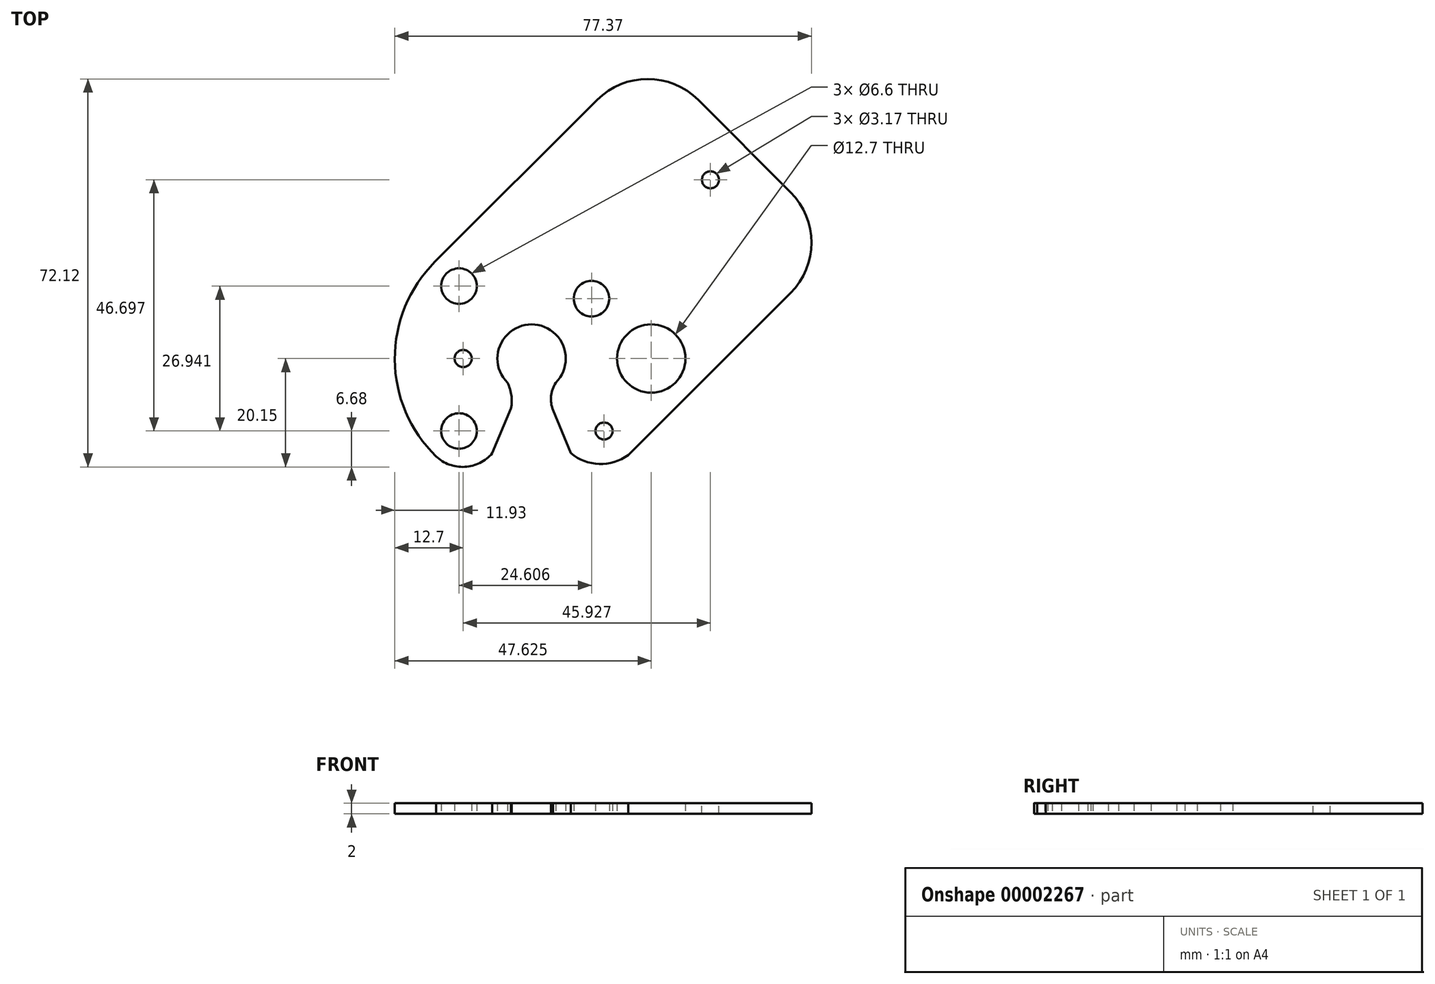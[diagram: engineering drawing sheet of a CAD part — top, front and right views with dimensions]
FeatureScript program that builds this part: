
annotation { "Feature Type Name" : "Feature", "Feature Type Description" : "" }
export const myFeature = defineFeature(function(context is Context, id is Id, definition is map)
    precondition{}
    {
        {
            var Q0;
            Q0=qCreatedBy(makeId("Top.planeOp"),FACE);
            var sketch = newSketch(context, id + "F0", { "sketchPlane" : qUnion([Q0])});
            skCircle(sketch, "E0", {"center": v(0, 0) * mm, "radius": 25.4 * mm});
            skCircle(sketch, "E1", {"center": v(0, 0) * mm, "radius": 6.35 * mm});
            skCircle(sketch, "E2", {"center": v(0, 0) * mm, "radius": 19.05 * mm, "construction": true});
            skLineSegment(sketch, "E3", {"start": v(0, 25.4) * mm, "end": v(0, -25.4) * mm, "construction": true});
            skLineSegment(sketch, "E4", {"start": v(25.4, 0) * mm, "end": v(-25.4, 0) * mm});
            skLineSegment(sketch, "E5", {"start": v(0, 0) * mm, "end": v(-26.94, -26.94) * mm});
            skLineSegment(sketch, "E6.2.0", {"start": v(0, 0) * mm, "end": v(26.94, 26.94) * mm, "construction": true});
            skLineSegment(sketch, "E6.3.0", {"start": v(0, 0) * mm, "end": v(-26.94, 26.94) * mm, "construction": true});
            skPoint(sketch, "E7", {"position": v(13.47, 13.47) * mm});
            skPoint(sketch, "E8", {"position": v(-13.47, 13.47) * mm});
            skPoint(sketch, "E9", {"position": v(13.47, -13.47) * mm});
            skPoint(sketch, "E10", {"position": v(-13.47, -13.47) * mm});
            skLineSegment(sketch, "E11", {"start": v(0, 0) * mm, "end": v(9.72, -23.47) * mm});
            skLineSegment(sketch, "E12.MirrorCS", {"start": v(-17.96, 17.96) * mm, "end": v(17.96, -17.96) * mm, "construction": true});
            skLineSegment(sketch, "E13.MirrorCS", {"start": v(0, 0) * mm, "end": v(-9.72, -23.47) * mm});
            skPoint(sketch, "E14", {"position": v(-7.3, -17.6) * mm});
            skPoint(sketch, "E15", {"position": v(7.3, -17.6) * mm});
            skArc(sketch, "E16", {"start": v(-17.96, -17.96) * mm, "mid": v(-12.55, -20.14) * mm, "end": v(-7.3, -17.6) * mm});
            skArc(sketch, "E17", {"start": v(7.3, -17.6) * mm, "mid": v(12.56, -19.59) * mm, "end": v(17.96, -17.96) * mm});
            skCircle(sketch, "E18", {"center": v(13.47, 13.47) * mm, "radius": 3.3 * mm, "construction": true});
            skCircle(sketch, "E19", {"center": v(-13.47, 13.47) * mm, "radius": 3.3 * mm});
            skCircle(sketch, "E20", {"center": v(-13.47, -13.47) * mm, "radius": 3.3 * mm});
            skCircle(sketch, "E21", {"center": v(13.47, -13.47) * mm, "radius": 1.59 * mm});
            skCircle(sketch, "E22", {"center": v(-12.7, 0) * mm, "radius": 1.59 * mm});
            skCircle(sketch, "E23", {"center": v(22.23, 0) * mm, "radius": 6.35 * mm});
            skPoint(sketch, "E24", {"position": v(18.37, 5.05) * mm});
            skPoint(sketch, "E25", {"position": v(18.37, -5.05) * mm});
            skPoint(sketch, "E26", {"position": v(22.71, -11.37) * mm});
            skPoint(sketch, "E27", {"position": v(22.71, 11.37) * mm});
            skArc(sketch, "E28", {"start": v(4.5, -4.5) * mm, "mid": v(3.61, -7.14) * mm, "end": v(4.1, -9.88) * mm});
            skArc(sketch, "E29", {"start": v(-4.86, -11.73) * mm, "mid": v(-3.69, -8.16) * mm, "end": v(-4.5, -4.5) * mm});
            skPoint(sketch, "E30", {"position": v(11.14, 11.14) * mm});
            skCircle(sketch, "E31", {"center": v(11.14, 11.14) * mm, "radius": 3.3 * mm});
            skLineSegment(sketch, "E32", {"start": v(26.94, 26.94) * mm, "end": v(44.9, 8.98) * mm});
            skLineSegment(sketch, "E33", {"start": v(44.9, 8.98) * mm, "end": v(17.96, -17.96) * mm});
            skLineSegment(sketch, "E34.MirrorCS", {"start": v(26.94, 26.94) * mm, "end": v(8.98, 44.9) * mm});
            skLineSegment(sketch, "E35.MirrorCS", {"start": v(8.98, 44.9) * mm, "end": v(-17.96, 17.96) * mm});
            skCircle(sketch, "E36", {"center": v(11.14, 11.14) * mm, "radius": 1.59 * mm});
            skCircle(sketch, "E37", {"center": v(-13.47, 13.47) * mm, "radius": 1.59 * mm});
            skCircle(sketch, "E38", {"center": v(-13.47, -13.47) * mm, "radius": 1.59 * mm});
            skSolve(sketch);
        }
        {
            var Q0;
            {var subQ0=sQuery(id+"F0.wireOp",EDGE,"E4");var subQ1=sQuery(id+"F0.wireOp",EDGE,"E0");var subQ2=makeQuery(id+"F0.imprint","INTERSECT",VERTEX,{"disambiguationData":[OD(0.0)],"derivedFrom":[subQ1,subQ0]});Q0=makeQuery(id+"F0.imprint","IMPRINT",FACE,{"disambiguationData":[TD([[makeQuery(id+"F0.imprint","IMPRINT",EDGE,{"disambiguationData":[TD([[subQ2,-1.0]])],"derivedFrom":subQ1}),1.0]])]});}
            var Q1;
            {var subQ0=sQuery(id+"F0.wireOp",EDGE,"E4");var subQ1=sQuery(id+"F0.wireOp",EDGE,"E0");var subQ2=makeQuery(id+"F0.imprint","INTERSECT",VERTEX,{"disambiguationData":[OD(0.0)],"derivedFrom":[subQ1,subQ0]});Q1=makeQuery(id+"F0.imprint","IMPRINT",FACE,{"disambiguationData":[TD([[makeQuery(id+"F0.imprint","IMPRINT",EDGE,{"disambiguationData":[TD([[subQ2,1.0]])],"derivedFrom":subQ1}),1.0]])]});}
            var Q2;
            Q2=makeQuery(id+"F0.imprint","IMPRINT",FACE,{"disambiguationData":[TD([[makeQuery(id+"F0.imprint","IMPRINT",EDGE,{"derivedFrom":sQuery(id+"F0.wireOp",EDGE,"E19")}),-1.0]])]});
            var Q3;
            {var subQ9=sQuery(id+"F0.wireOp",EDGE,"E17");Q3=makeQuery(id+"F0.imprint","IMPRINT",FACE,{"disambiguationData":[TD([[makeQuery(id+"F0.imprint","IMPRINT",EDGE,{"derivedFrom":subQ9}),1.0]])]});}
            var Q4;
            {var subQ7=sQuery(id+"F0.wireOp",EDGE,"E29");var subQ8=sQuery(id+"F0.wireOp",EDGE,"E13.MirrorCS");var subQ9=makeQuery(id+"F0.imprint","INTERSECT",VERTEX,{"disambiguationData":[OD(0.0)],"derivedFrom":[subQ8,subQ7]});Q4=makeQuery(id+"F0.imprint","IMPRINT",FACE,{"disambiguationData":[TD([[makeQuery(id+"F0.imprint","IMPRINT",EDGE,{"disambiguationData":[TD([[subQ9,1.0]])],"derivedFrom":subQ8}),-1.0]])]});}
            var Q5;
            {var subQ0=sQuery(id+"F0.wireOp",EDGE,"E4");var subQ6=sQuery(id+"F0.wireOp",EDGE,"E1");var subQ8=makeQuery(id+"F0.imprint","INTERSECT",VERTEX,{"disambiguationData":[OD(0.0)],"derivedFrom":[subQ6,subQ0]});Q5=makeQuery(id+"F0.imprint","IMPRINT",FACE,{"disambiguationData":[TD([[makeQuery(id+"F0.imprint","IMPRINT",EDGE,{"disambiguationData":[TD([[subQ8,-1.0]])],"derivedFrom":subQ0}),1.0]])]});}
            var Q6;
            Q6=makeQuery(id+"F0.imprint","IMPRINT",FACE,{"disambiguationData":[TD([[makeQuery(id+"F0.imprint","IMPRINT",EDGE,{"derivedFrom":sQuery(id+"F0.wireOp",EDGE,"E32")}),-1.0]])]});
            var Q7;
            {var subQ0=sQuery(id+"F0.wireOp",EDGE,"E0");var subQ1=makeQuery(id+"F0.imprint","INTERSECT",VERTEX,{"disambiguationData":[OD(0.0)],"derivedFrom":[subQ0,sQuery(id+"F0.wireOp",EDGE,"E4")]});Q7=makeQuery(id+"F0.imprint","IMPRINT",FACE,{"disambiguationData":[TD([[makeQuery(id+"F0.imprint","IMPRINT",EDGE,{"disambiguationData":[TD([[subQ1,-1.0]])],"derivedFrom":subQ0}),-1.0]])]});}
            extrude(context, id + "F1", {"entities" : qUnion([Q0, Q1, Q2, Q3, Q4, Q5, Q6, Q7]), "depth" : 2 * mm, "offsetDistance" : 25 * mm});
        }
        {
            var Q0;
            Q0=makeQuery(id+"F1.opExtrude","SWEPT_FACE",FACE,{"disambiguationData":[OSD([sQuery(id+"F0.wireOp",EDGE,"E32"),sQuery(id+"F0.wireOp",EDGE,"E34.MirrorCS")])]});
            extrude(context, id + "F2", {"entities" : qUnion([Q0]), "operationType" : NewBodyOperationType.ADD, "depth" : 17.78 * mm, "offsetDistance" : 25 * mm});
        }
        {
            var Q0;
            Q0=makeQuery(id+"F2.opExtrude","CAP_EDGE",EDGE,{"disambiguationData":[OSD([sQuery(id+"F0.wireOp",EDGE,"E32"),sQuery(id+"F0.wireOp",EDGE,"E33")])],"isStart":false});
            var Q1;
            Q1=makeQuery(id+"F2.opExtrude","CAP_EDGE",EDGE,{"disambiguationData":[OSD([sQuery(id+"F0.wireOp",EDGE,"E34.MirrorCS"),sQuery(id+"F0.wireOp",EDGE,"E35.MirrorCS")])],"isStart":false});
            fillet(context, id + "F3", {"entities" : qUnion([Q0, Q1]), "radius" : 13.28 * mm, "tangentPropagation" : true, "allowEdgeOverflow" : false});
        }
        {
            var Q0;
            {var subQ0=sQuery(id+"F0.wireOp",EDGE,"E34.MirrorCS");var subQ1=sQuery(id+"F0.wireOp",EDGE,"E32");Q0=makeQuery(id+"F2.boolean.opBoolean","MERGE",FACE,{"derivedFrom":[makeQuery(id+"F1.opExtrude","CAP_FACE",FACE,{"disambiguationData":[OSD([sQuery(id+"F0.wireOp",EDGE,"E0"),sQuery(id+"F0.wireOp",EDGE,"E1"),sQuery(id+"F0.wireOp",EDGE,"E11"),sQuery(id+"F0.wireOp",EDGE,"E13.MirrorCS"),sQuery(id+"F0.wireOp",EDGE,"E16"),sQuery(id+"F0.wireOp",EDGE,"E17"),sQuery(id+"F0.wireOp",EDGE,"E19"),sQuery(id+"F0.wireOp",EDGE,"E20"),sQuery(id+"F0.wireOp",EDGE,"E21"),sQuery(id+"F0.wireOp",EDGE,"E22"),sQuery(id+"F0.wireOp",EDGE,"E28"),sQuery(id+"F0.wireOp",EDGE,"E29"),sQuery(id+"F0.wireOp",EDGE,"E31"),subQ1,sQuery(id+"F0.wireOp",EDGE,"E33"),subQ0,sQuery(id+"F0.wireOp",EDGE,"E35.MirrorCS")])],"isStart":false}),makeQuery(id+"F2.opExtrude","SWEPT_FACE",FACE,{"disambiguationData":[OSD([subQ1,subQ0]),TDD([makeQuery(id+"F1.opExtrude","CAP_EDGE",EDGE,{"disambiguationData":[OSD([subQ1,subQ0])],"isStart":false})])]})]});}
            var sketch = newSketch(context, id + "F4", { "sketchPlane" : qUnion([Q0])});
            skLineSegment(sketch, "E39", {"start": v(39.51, 39.51) * mm, "end": v(11.14, 11.14) * mm, "construction": true});
            skCircle(sketch, "E40", {"center": v(33.23, 33.23) * mm, "radius": 1.59 * mm});
            skSolve(sketch);
        }
        {
            var Q0;
            Q0=makeQuery(id+"F4.imprint","IMPRINT",FACE,{"disambiguationData":[TD([[makeQuery(id+"F4.imprint","IMPRINT",EDGE,{"derivedFrom":sQuery(id+"F4.wireOp",EDGE,"E40")}),1.0]])]});
            extrude(context, id + "F5", {"entities" : qUnion([Q0]), "operationType" : NewBodyOperationType.REMOVE, "endBound" : BoundingType.UP_TO_NEXT, "oppositeDirection" : true, "depth" : 25 * mm, "offsetDistance" : 25 * mm});
        }
    });
